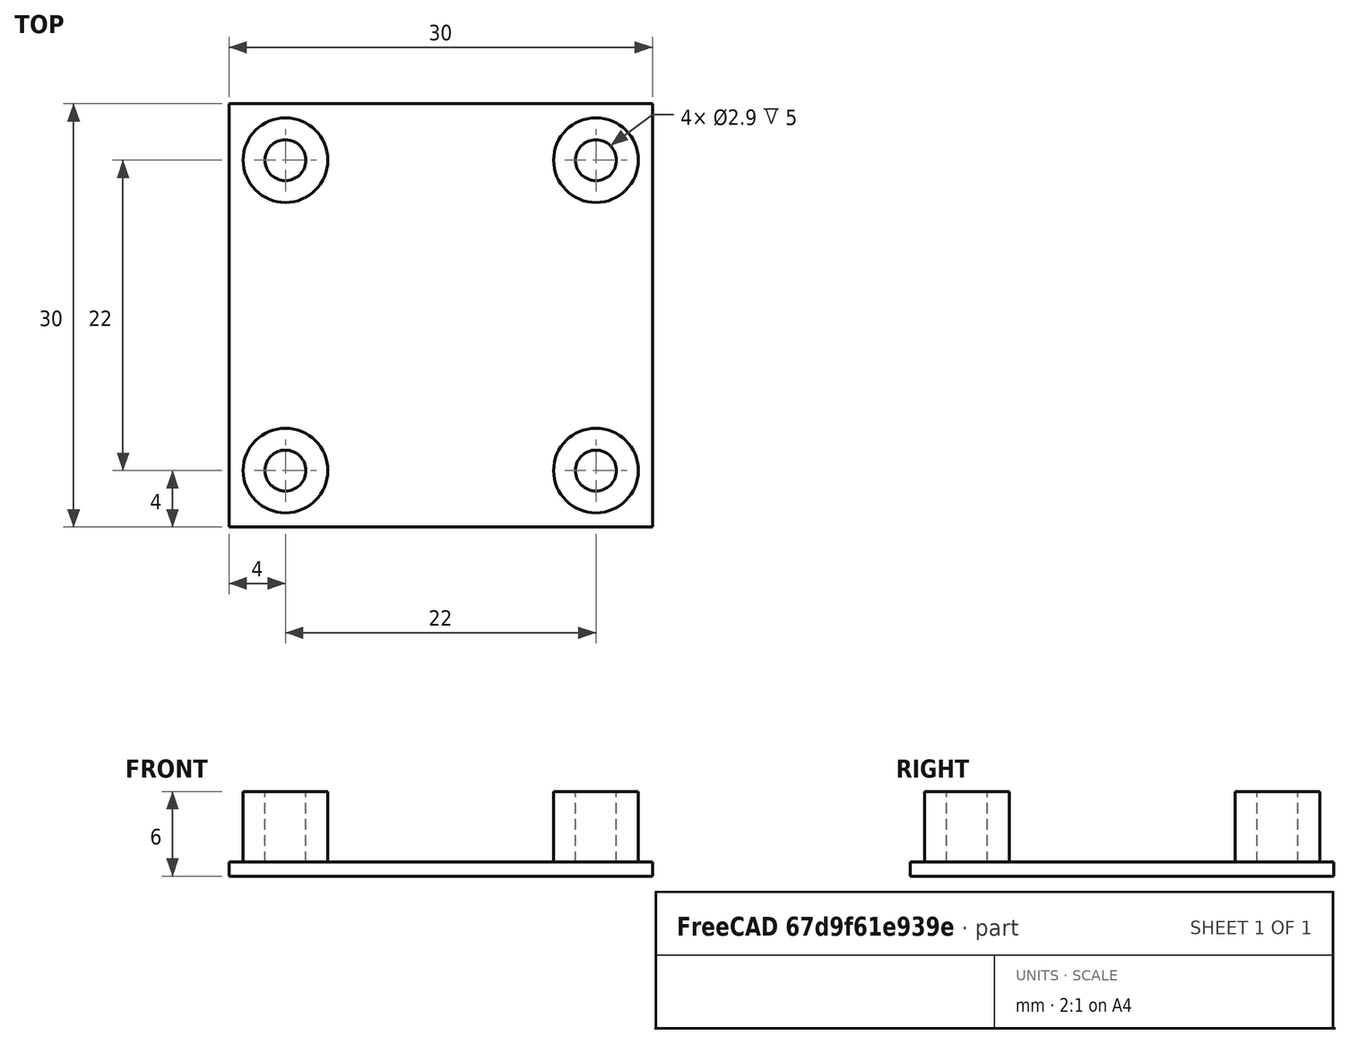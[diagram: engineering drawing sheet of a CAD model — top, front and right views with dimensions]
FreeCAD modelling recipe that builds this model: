
FCSTD DOCUMENT  (FreeCAD 1.0R39285 (Git))
Label: HBridge Mount
License: All rights reserved
LicenseURL: https://en.wikipedia.org/wiki/All_rights_reserved
objects: Part::FeaturePython×5, Part::Box×1, Part::MultiFuse×1
note: 7 computed .brp shape members not serialized (recipe doc carries the construction recipe); baked Part::Feature solids carry a one-line shape summary decoded from their .brp

FEATURE [Part::FeaturePython] Tube002  # WARN: FeaturePython — macro-defined, semantics opaque (R4)
  AttacherType = Attacher::AttachEngine3D
  Height = 5
  InnerRadius = 1.45
  OuterRadius = 3
  Placement = pos=(26,26,1) rot=(0,0,1;0rad)
FEATURE [Part::FeaturePython] Tube001  # WARN: FeaturePython — macro-defined, semantics opaque (R4)
  AttacherType = Attacher::AttachEngine3D
  Height = 5
  InnerRadius = 1.45
  OuterRadius = 3
  Placement = pos=(26,4,1) rot=(0,0,1;0rad)
FEATURE [Part::FeaturePython] Tube  # WARN: FeaturePython — macro-defined, semantics opaque (R4)
  AttacherType = Attacher::AttachEngine3D
  Height = 5
  InnerRadius = 1.45
  OuterRadius = 3
  Placement = pos=(4,4,1) rot=(0,0,1;0rad)
FEATURE [Part::Box] Box006  label="Cube"
  AttacherType = Attacher::AttachEngine3D
  Height = 1
  Length = 30
  Width = 30
FEATURE [Part::FeaturePython] Tube003  # WARN: FeaturePython — macro-defined, semantics opaque (R4)
  AttacherType = Attacher::AttachEngine3D
  Height = 5
  InnerRadius = 1.45
  OuterRadius = 3
  Placement = pos=(4,26,1) rot=(0,0,1;0rad)
FEATURE [Part::MultiFuse] Fusion003  label="H Bridge Mount"
  Shapes = -> [Tube003,Box006,Tube,Tube001,Tube002]
FEATURE [Part::FeaturePython] Clone  label="H Bridge Mount001"  # Draft clone (typed FeaturePython)
  AttacherType = Attacher::AttachEngine3D
  Fuse = false
  Objects = -> [Fusion003]
  Scale = (1,1,1)
